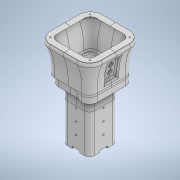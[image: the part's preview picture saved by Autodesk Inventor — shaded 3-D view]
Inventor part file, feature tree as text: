
AUTODESK INVENTOR PART (.ipt)
format: ipt  version: 2021 (Build 250183000, 183)  size: 2,477,056 bytes
history: native  units: mm
features: sketch x27, other x24, extrude x14, projected_geometry x14, hole x9, plane x5, chamfer x4, mirror x4, fillet x3, loft x2, shell x1, sweep x1, pattern_circular x1
ambient origin geometry x8: Origin, YZ Plane, XZ Plane, XY Plane, X Axis, Y Axis, Z Axis, Center Point
bodies: Body1 (feature_tree), Body2 (feature_tree), Body3 (feature_tree), Body4 (feature_tree), Body5 (feature_tree), Body6 (feature_tree), Body7 (feature_tree), Body8 (feature_tree), Body9 (feature_tree), Body10 (feature_tree)
feature tree (109):
  other  "實體1"
  sketch  "草圖1"
  plane  "工作平面1"
  sketch  "草圖2"
  extrude  "擠出1"  Depth=139.0mm
  loft  "斷面混成1"
  extrude  "擠出2"  Depth=25.0mm
  plane  "工作平面2"
  extrude  "擠出6"  Depth=30.0mm
  loft  "斷面混成3"
  chamfer  "倒角2"  Distance=205.0mm
  fillet  "圓角3"  Radius=45.0mm
  extrude  "擠出7"  Depth=230.0mm TaperAngle=0.0deg
  fillet  "圓角4"  [1 undecoded]
  shell  "薄殼2"  Thickness=0.0mm
  chamfer  "倒角1"  Distance=200.0mm
  extrude  "擠出9"  [1 undecoded]
  chamfer  "倒角4"  Distance=220.0mm
  hole  "孔4"  [1 undecoded]
  sweep  "掃掠3"
  hole  "孔6"  [1 undecoded]
  extrude  "擠出10"  Depth=30.0mm
  plane  "工作平面3"
  extrude  "擠出11"  Depth=10.0mm TaperAngle=75.0deg
  fillet  "圓角5"  Radius=20.0mm
  hole  "孔7"  [1 undecoded]
  extrude  "擠出13"  Depth=50.0mm
  extrude  "擠出14"  Depth=40.0mm TaperAngle=0.0deg
  extrude  "擠出15"  Depth=20.0mm
  hole  "孔8"  [1 undecoded]
  mirror  "鏡射1"
  mirror  "鏡射2"
  extrude  "擠出16"  Depth=7.0mm TaperAngle=45.0deg
  extrude  "擠出17"  Depth=10.0mm TaperAngle=45.0deg
  mirror  "鏡射3"
  mirror  "鏡射4"
  hole  "孔9"  [1 undecoded]
  hole  "孔10"  [1 undecoded]
  pattern_circular  "環形陣列2"  [2 undecoded]
  extrude  "擠出18"  Depth=20.0mm TaperAngle=45.0deg
  hole  "孔11"  [1 undecoded]
  plane  "工作平面4"
  plane  "工作平面5"
  other  "分割1"
  other  "分割2"
  other  "分割3"
  other  "分割4"
  other  "分割5"
  other  "分割6"
  sketch  "草圖43"
  hole  "孔12"  [1 undecoded]
  hole  "孔13"  [1 undecoded]
  extrude  "擠出19"  TaperAngle=45.0deg  [1 undecoded]
  chamfer  "倒角5"  [1 undecoded]
  sketch  "草圖3"
  projected_geometry  "投影迴路1"
  sketch  "草圖17"
  sketch  "草圖18"
  projected_geometry  "投影迴路7"
  sketch  "草圖20"
  projected_geometry  "投影迴路9"
  sketch  "草圖23"
  projected_geometry  "投影迴路10"
  sketch  "草圖24"
  sketch  "草圖25"
  sketch  "3D 草圖2"
  sketch  "草圖27"
  sketch  "草圖28"
  other  "Srf1"
  sketch  "草圖29"
  sketch  "草圖30"
  projected_geometry  "投影迴路11"
  sketch  "草圖31"
  sketch  "草圖33"
  projected_geometry  "投影迴路14"
  sketch  "草圖34"
  projected_geometry  "投影迴路15"
  sketch  "草圖35"
  projected_geometry  "投影迴路16"
  sketch  "草圖36"
  sketch  "草圖37"
  projected_geometry  "投影迴路17"
  other  "實體3"
  sketch  "草圖38"
  sketch  "草圖39"
  sketch  "草圖40"
  sketch  "草圖41"
  projected_geometry  "投影迴路18"
  other  "實體4"
  sketch  "草圖42"
  projected_geometry  "投影迴路19"
  projected_geometry  "投影迴路20"
  projected_geometry  "投影迴路21"
  sketch  "草圖44"
  projected_geometry  "投影迴路22"
  other  "擠出表面1"
  other  "投影切割邊5"
  other  "實體5"
  other  "實體6"
  other  "實體7"
  other  "實體8"
  other  "實體9"
  other  "實體10"
  other  "實體11"
  other  "實體12"
  other  "實體13"
  other  "實體14"
  other  "實體15"
  other  "實體16"
note: 15 required parameter values undecoded (feature->parameter linkage not recoverable at this tier; creation-order binding heuristic only, values carry confidence <= 0.55)
